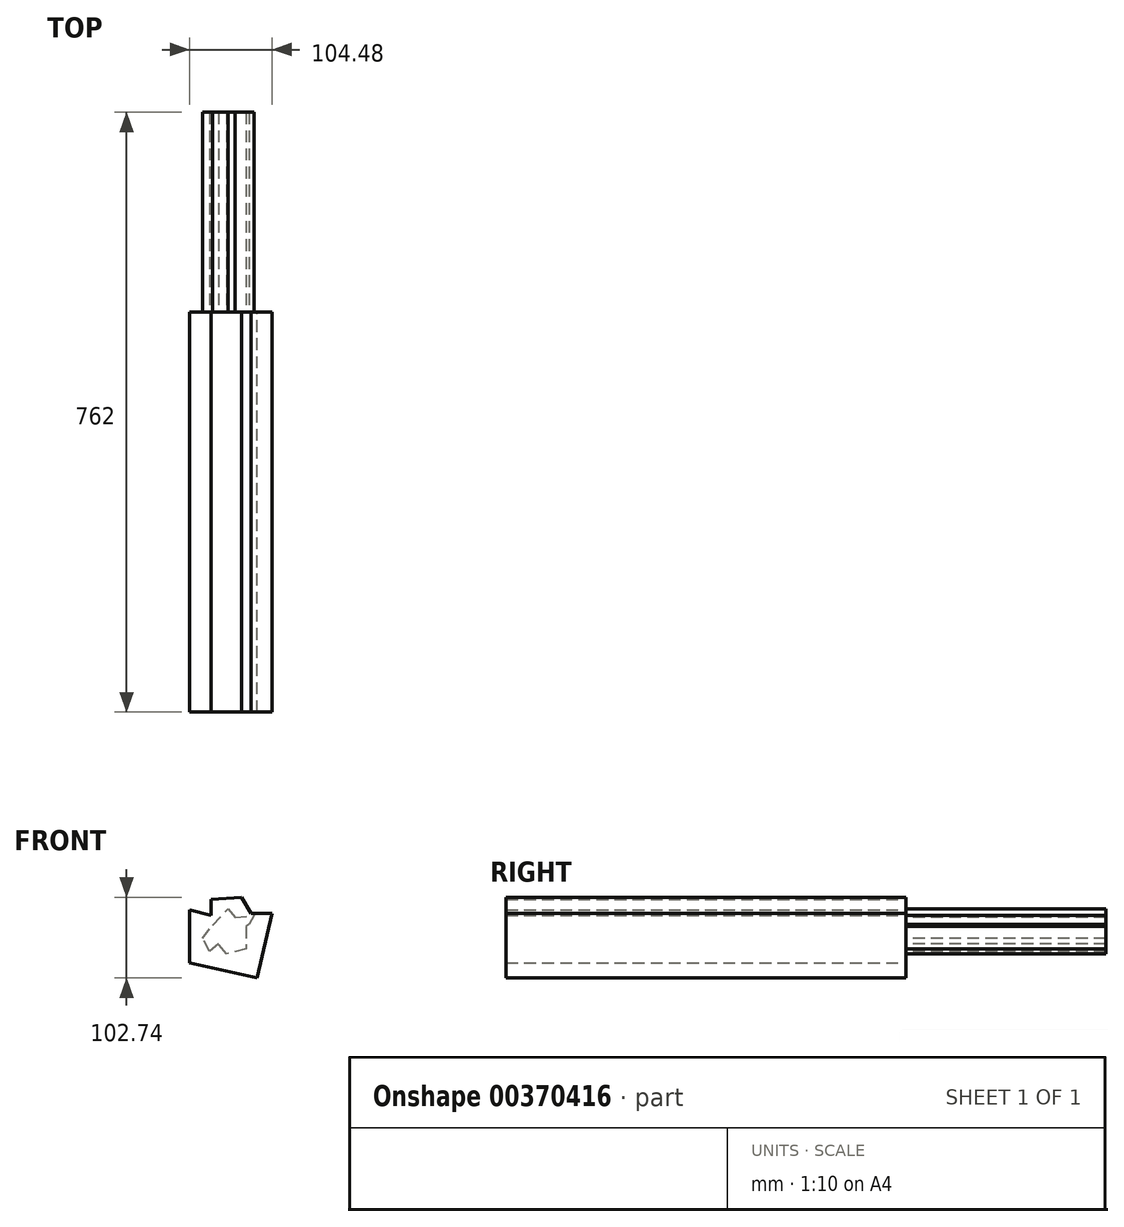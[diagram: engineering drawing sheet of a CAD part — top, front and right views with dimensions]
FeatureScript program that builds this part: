
annotation { "Feature Type Name" : "Feature", "Feature Type Description" : "" }
export const myFeature = defineFeature(function(context is Context, id is Id, definition is map)
    precondition{}
    {
        {
            var Q0;
            Q0=qCreatedBy(makeId("Front.planeOp"),FACE);
            var sketch = newSketch(context, id + "F0", { "sketchPlane" : qUnion([Q0])});
            skLineSegment(sketch, "E0", {"start": v(-50.26, 35.85) * mm, "end": v(-50.26, -33.63) * mm});
            skLineSegment(sketch, "E1", {"start": v(-50.26, -33.63) * mm, "end": v(35.48, -53.22) * mm});
            skLineSegment(sketch, "E2", {"start": v(35.48, -53.22) * mm, "end": v(54.22, 28.84) * mm});
            skLineSegment(sketch, "E3", {"start": v(54.22, 28.84) * mm, "end": v(28.09, 28.84) * mm});
            skLineSegment(sketch, "E4", {"start": v(28.09, 28.84) * mm, "end": v(15.9, 49.52) * mm});
            skLineSegment(sketch, "E5", {"start": v(15.9, 49.52) * mm, "end": v(-22.91, 46.93) * mm});
            skLineSegment(sketch, "E6", {"start": v(-22.91, 46.93) * mm, "end": v(-22.91, 26.24) * mm});
            skLineSegment(sketch, "E7", {"start": v(-22.91, 26.24) * mm, "end": v(-51, 33.63) * mm});
            skSolve(sketch);
        }
        {
            var Q0;
            {var subQ0=sQuery(id+"F0.wireOp",EDGE,"E1");Q0=makeQuery(id+"F0.imprint","IMPRINT",FACE,{"disambiguationData":[TD([[makeQuery(id+"F0.imprint","IMPRINT",EDGE,{"derivedFrom":subQ0}),1.0]])]});}
            extrude(context, id + "F1", {"entities" : qUnion([Q0]), "depth" : 508 * mm});
        }
        {
            var Q0;
            Q0=makeQuery(id+"F1.opExtrude","CAP_FACE",FACE,{"disambiguationData":[OSD([sQuery(id+"F0.wireOp",EDGE,"E0"),sQuery(id+"F0.wireOp",EDGE,"E1"),sQuery(id+"F0.wireOp",EDGE,"E2"),sQuery(id+"F0.wireOp",EDGE,"E3"),sQuery(id+"F0.wireOp",EDGE,"E4"),sQuery(id+"F0.wireOp",EDGE,"E5"),sQuery(id+"F0.wireOp",EDGE,"E6"),sQuery(id+"F0.wireOp",EDGE,"E7")])],"isStart":true});
            var sketch = newSketch(context, id + "F2", { "sketchPlane" : qUnion([Q0])});
            skLineSegment(sketch, "E8", {"start": v(-5.88, 11.14) * mm, "end": v(28.59, 10.8) * mm});
            skLineSegment(sketch, "E9", {"start": v(28.59, 10.8) * mm, "end": v(31.26, -10.76) * mm});
            skLineSegment(sketch, "E10", {"start": v(31.26, -10.76) * mm, "end": v(16.7, -22.7) * mm});
            skLineSegment(sketch, "E11", {"start": v(16.7, -22.7) * mm, "end": v(0, -22.7) * mm});
            skLineSegment(sketch, "E12", {"start": v(0, -22.7) * mm, "end": v(-25.93, -8.41) * mm});
            skLineSegment(sketch, "E13", {"start": v(-25.93, -8.41) * mm, "end": v(-24.07, 12.26) * mm});
            skLineSegment(sketch, "E14", {"start": v(-24.07, 12.26) * mm, "end": v(-6.95, 10.14) * mm});
            skLineSegment(sketch, "E15", {"start": v(-6.95, 10.14) * mm, "end": v(-5.88, 11.14) * mm});
            skSolve(sketch);
        }
        {
            var Q0;
            Q0=makeQuery(id+"F2.imprint","IMPRINT",FACE,{"disambiguationData":[TD([[makeQuery(id+"F2.imprint","IMPRINT",EDGE,{"derivedFrom":sQuery(id+"F2.wireOp",EDGE,"E8")}),-1.0]])]});
            extrude(context, id + "F3", {"entities" : qUnion([Q0]), "operationType" : NewBodyOperationType.ADD, "oppositeDirection" : true, "depth" : 254 * mm});
        }
        {
            var Q0;
            Q0=qCreatedBy(makeId("Front.planeOp"),FACE);
            var sketch = newSketch(context, id + "F4", { "sketchPlane" : qUnion([Q0])});
            skLineSegment(sketch, "E16", {"start": v(21.64, 12.29) * mm, "end": v(21.64, -16.15) * mm});
            skLineSegment(sketch, "E17", {"start": v(21.64, -16.15) * mm, "end": v(-3.47, -22.47) * mm});
            skLineSegment(sketch, "E18", {"start": v(-3.47, -22.47) * mm, "end": v(-13.62, -10) * mm});
            skLineSegment(sketch, "E19", {"start": v(-13.62, -10) * mm, "end": v(-24.76, -19.14) * mm});
            skLineSegment(sketch, "E20", {"start": v(-24.76, -19.14) * mm, "end": v(-33.9, -2.85) * mm});
            skLineSegment(sketch, "E21", {"start": v(-33.9, -2.85) * mm, "end": v(-20.94, 13.62) * mm});
            skLineSegment(sketch, "E22", {"start": v(-20.94, 13.62) * mm, "end": v(-1.64, 34.57) * mm});
            skLineSegment(sketch, "E23", {"start": v(-1.64, 34.57) * mm, "end": v(7.34, 23.93) * mm});
            skLineSegment(sketch, "E24", {"start": v(7.34, 23.93) * mm, "end": v(31.61, 26.25) * mm});
            skLineSegment(sketch, "E25", {"start": v(31.61, 26.25) * mm, "end": v(25.46, 15.11) * mm});
            skLineSegment(sketch, "E26", {"start": v(25.46, 15.11) * mm, "end": v(21.64, 12.29) * mm});
            skSolve(sketch);
        }
        {
            var Q0;
            Q0=makeQuery(id+"F4.imprint","IMPRINT",FACE,{"disambiguationData":[TD([[makeQuery(id+"F4.imprint","IMPRINT",EDGE,{"derivedFrom":sQuery(id+"F4.wireOp",EDGE,"E16")}),-1.0]])]});
            extrude(context, id + "F5", {"entities" : qUnion([Q0]), "operationType" : NewBodyOperationType.ADD, "oppositeDirection" : true, "depth" : 254 * mm});
        }
    });
